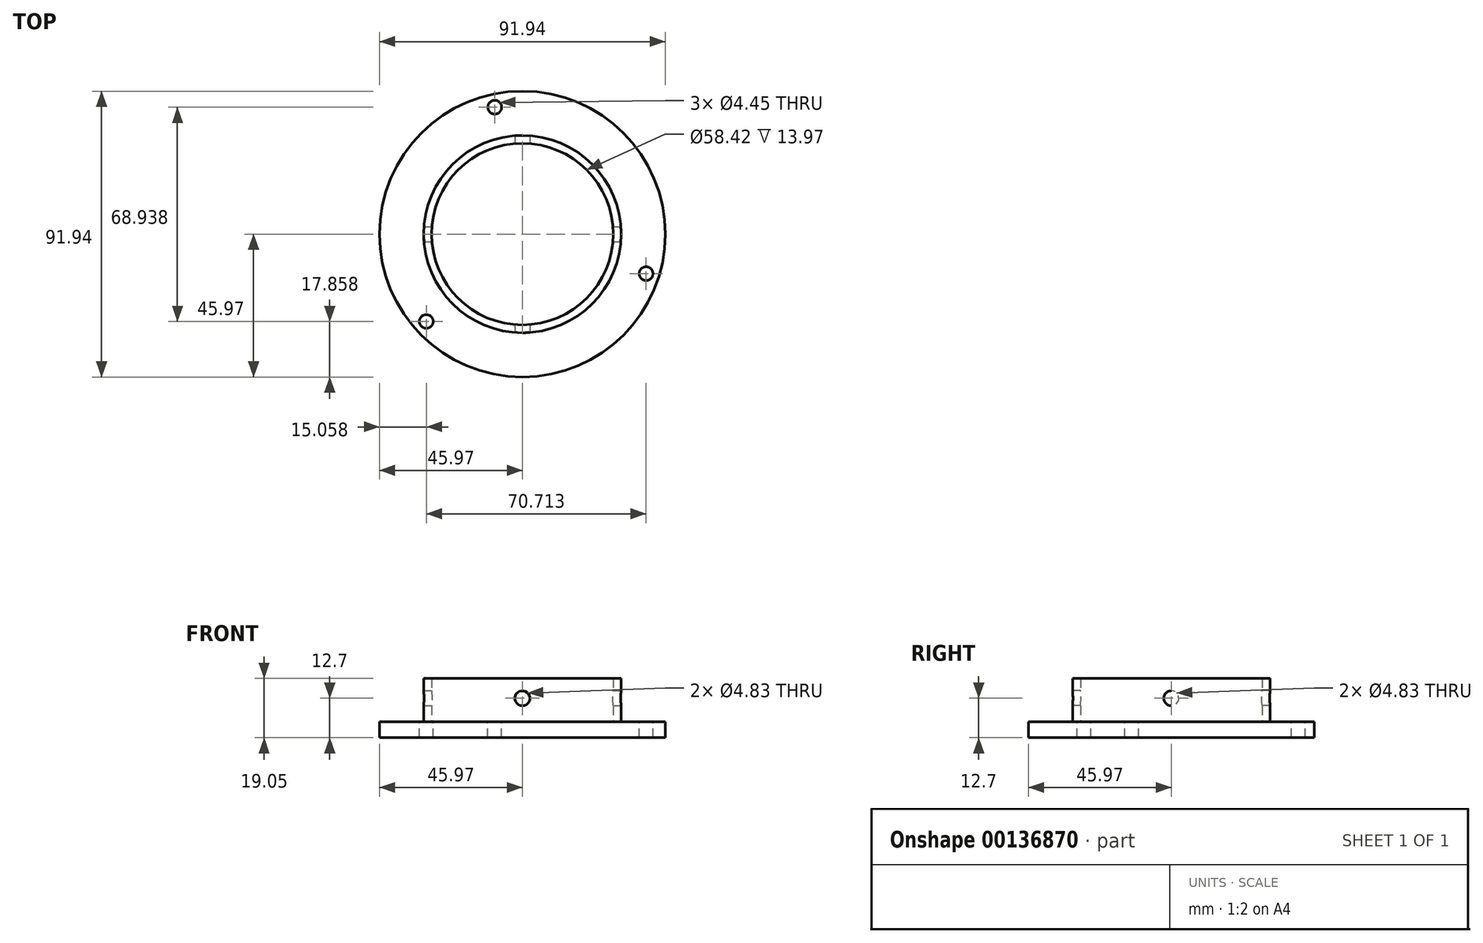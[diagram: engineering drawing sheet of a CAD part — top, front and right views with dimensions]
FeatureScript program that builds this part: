
annotation { "Feature Type Name" : "Feature", "Feature Type Description" : "" }
export const myFeature = defineFeature(function(context is Context, id is Id, definition is map)
    precondition{}
    {
        {
            var Q0;
            Q0=qCreatedBy(makeId("Top.planeOp"),FACE);
            var sketch = newSketch(context, id + "F0", { "sketchPlane" : qUnion([Q0])});
            skCircle(sketch, "E0", {"center": v(0, 0) * mm, "radius": 29.21 * mm});
            skCircle(sketch, "E1", {"center": v(0, 0) * mm, "radius": 31.75 * mm});
            skSolve(sketch);
        }
        {
            var Q0;
            Q0=qSketchRegion(id+"F0",true);
            extrude(context, id + "F1", {"entities" : qUnion([Q0]), "depth" : 13.97 * mm});
        }
        {
            var Q0;
            Q0=qCreatedBy(makeId("Top.planeOp"),FACE);
            var sketch = newSketch(context, id + "F2", { "sketchPlane" : qUnion([Q0])});
            skLineSegment(sketch, "E2.bottom", {"start": v(44.45, -2.54) * mm, "end": v(-44.45, -2.54) * mm});
            skLineSegment(sketch, "E2.top", {"start": v(44.45, 2.54) * mm, "end": v(-44.45, 2.54) * mm});
            skLineSegment(sketch, "E2.left", {"start": v(44.45, -2.54) * mm, "end": v(44.45, 2.54) * mm});
            skLineSegment(sketch, "E2.right", {"start": v(-44.45, -2.54) * mm, "end": v(-44.45, 2.54) * mm});
            skPoint(sketch, "E2.middle", {"position": v(0, 0) * mm});
            skLineSegment(sketch, "E3", {"start": v(-31.65, 2.54) * mm, "end": v(-31.65, -2.54) * mm});
            skLineSegment(sketch, "E4", {"start": v(31.65, 2.54) * mm, "end": v(31.65, -2.54) * mm});
            skSolve(sketch);
        }
        {
            var Q0;
            Q0=qCreatedBy(makeId("Top.planeOp"),FACE);
            var sketch = newSketch(context, id + "F3", { "sketchPlane" : qUnion([Q0])});
            skLineSegment(sketch, "E5.bottom", {"start": v(-60.23, 0) * mm, "end": v(63.71, 0) * mm});
            skLineSegment(sketch, "E5.top", {"start": v(-60.23, -73.9) * mm, "end": v(63.71, -73.9) * mm});
            skLineSegment(sketch, "E5.left", {"start": v(-60.23, 0) * mm, "end": v(-60.23, -73.9) * mm});
            skLineSegment(sketch, "E5.right", {"start": v(63.71, 0) * mm, "end": v(63.71, -73.9) * mm});
            skSolve(sketch);
        }
        {
            var Q0;
            Q0=qCreatedBy(makeId("Top.planeOp"),FACE);
            var sketch = newSketch(context, id + "F4", { "sketchPlane" : qUnion([Q0])});
            skCircle(sketch, "E6", {"center": v(0, 0) * mm, "radius": 45.97 * mm});
            skSolve(sketch);
        }
        {
            var Q0;
            Q0=qSketchRegion(id+"F4",true);
            extrude(context, id + "F5", {"entities" : qUnion([Q0]), "operationType" : NewBodyOperationType.ADD, "oppositeDirection" : true, "depth" : 5.08 * mm});
        }
        {
            var Q0;
            Q0=qCreatedBy(makeId("Front.planeOp"),FACE);
            var sketch = newSketch(context, id + "F6", { "sketchPlane" : qUnion([Q0])});
            skCircle(sketch, "E7", {"center": v(0, 7.62) * mm, "radius": 2.41 * mm});
            skSolve(sketch);
        }
        {
            var Q0;
            Q0=qSketchRegion(id+"F6",true);
            extrude(context, id + "F7", {"entities" : qUnion([Q0]), "operationType" : NewBodyOperationType.REMOVE, "endBound" : BoundingType.SYMMETRIC, "oppositeDirection" : true, "depth" : 76.2 * mm});
        }
        {
            var Q0;
            {var subQ6=sQuery(id+"F4.wireOp",EDGE,"E6");Q0=makeQuery(id+"FT47Tx4rUoxAfJh_1.opDraft","SPLIT",FACE,{"disambiguationData":[OD(1.0)],"derivedFrom":makeQuery(id+"F5.boolean.opBoolean","SPLIT",FACE,{"disambiguationData":[TD([makeQuery(id+"F1.opExtrude","SWEPT_FACE",FACE,{"disambiguationData":[OSD([sQuery(id+"F0.wireOp",EDGE,"E1")])]})])],"derivedFrom":makeQuery(id+"F5.opExtrude","CAP_FACE",FACE,{"disambiguationData":[OSD([subQ6])],"isStart":true})})});}
            var sketch = newSketch(context, id + "F8", { "sketchPlane" : qUnion([Q0])});
            skPoint(sketch, "E8", {"position": v(-8.9, 40.83) * mm});
            skPoint(sketch, "E9.1.0", {"position": v(-30.91, -28.11) * mm});
            skPoint(sketch, "E9.2.0", {"position": v(39.8, -12.71) * mm});
            skPoint(sketch, "E9.center", {"position": v(0, 0) * mm});
            skSolve(sketch);
        }
        {
            var Q0;
            Q0=sQuery(id+"F8.wireOp",VERTEX,"E8");
            var Q1;
            Q1=sQuery(id+"F8.wireOp",VERTEX,"E9.1.0");
            var Q2;
            Q2=sQuery(id+"F8.wireOp",VERTEX,"E9.2.0");
            var Q3;
            Q3=makeQuery(id+"F1.opExtrude","SWEPT_BODY",BODY,{"disambiguationData":[OSD([sQuery(id+"F0.wireOp",EDGE,"E0"),sQuery(id+"F0.wireOp",EDGE,"E1")])]});
            hole(context, id + "F9", {"style" : HoleStyle.SIMPLE, "endStyle" : HoleEndStyle.BLIND, "holeDiameter" : 4.44 * mm, "holeDepth" : 12.7 * mm, "tappedDepth" : 12.7 * mm, "tapClearance" : 3, "startFromSketch" : true, "locations" : qUnion([Q0, Q1, Q2]), "scope" : qUnion([Q3])});
        }
        {
            var Q0;
            Q0=qCreatedBy(makeId("Right.planeOp"),FACE);
            var sketch = newSketch(context, id + "F10", { "sketchPlane" : qUnion([Q0])});
            skCircle(sketch, "E10", {"center": v(0, 7.62) * mm, "radius": 2.41 * mm});
            skSolve(sketch);
        }
        {
            var Q0;
            Q0 = qSketchRegion(id + "F10", true);
            extrude(context, id + "F11", {"entities" : qUnion([Q0]), "operationType" : NewBodyOperationType.REMOVE, "endBound" : BoundingType.SYMMETRIC, "oppositeDirection" : true, "depth" : 101.6 * mm});
        }
    });
